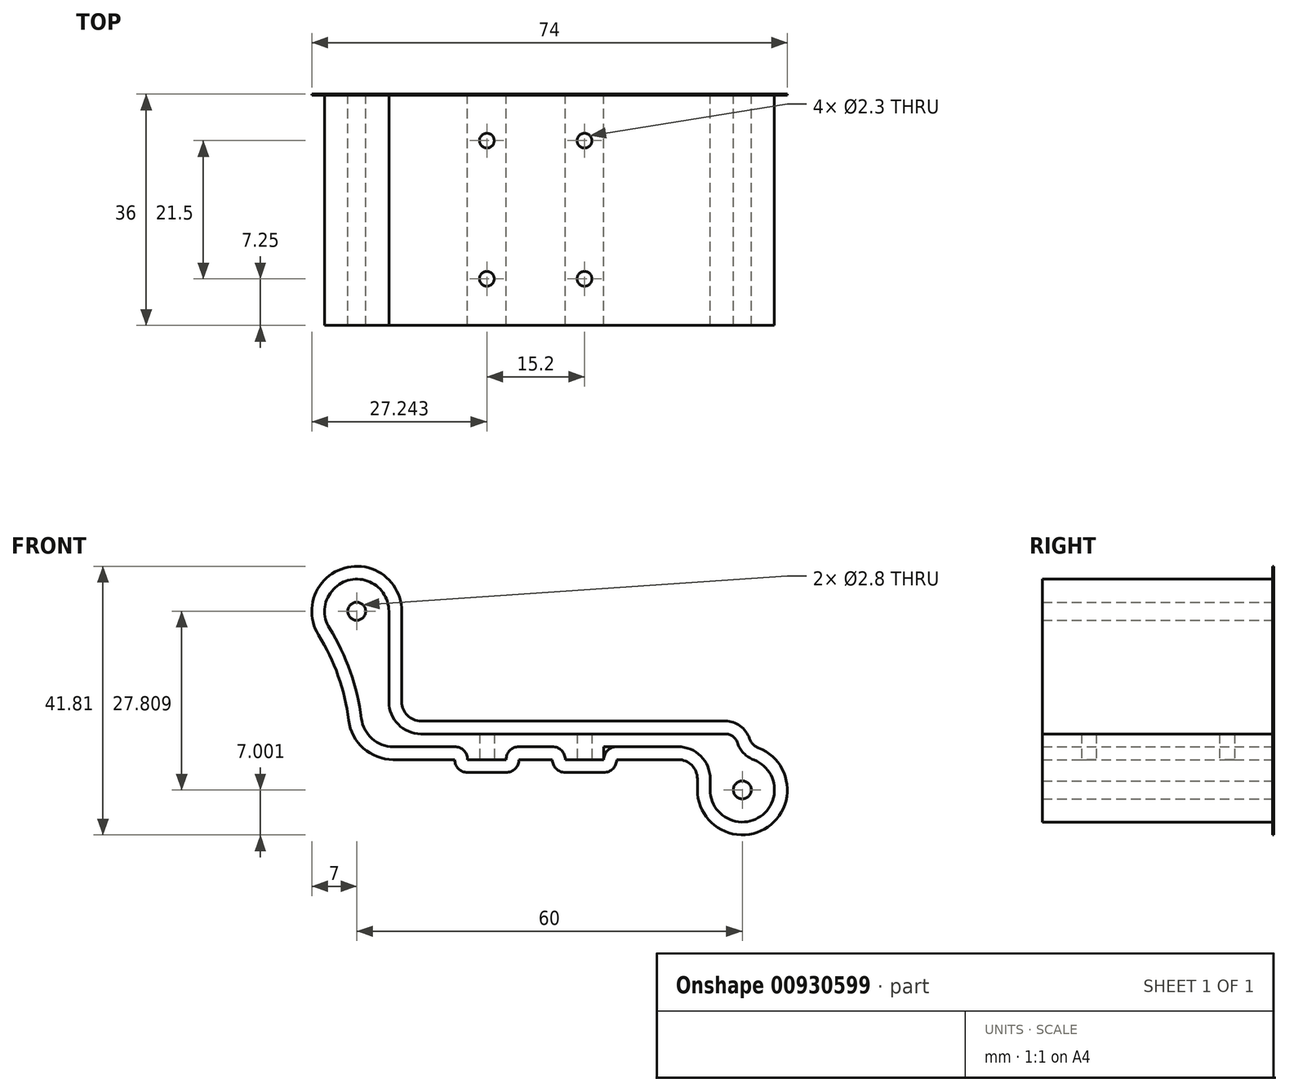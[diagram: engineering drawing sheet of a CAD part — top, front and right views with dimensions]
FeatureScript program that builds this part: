
annotation { "Feature Type Name" : "Feature", "Feature Type Description" : "" }
export const myFeature = defineFeature(function(context is Context, id is Id, definition is map)
    precondition{}
    {
        {
            var Q0;
            Q0=qCreatedBy(makeId("Front.planeOp"),FACE);
            var sketch = newSketch(context, id + "F0", { "sketchPlane" : qUnion([Q0])});
            skCircle(sketch, "E0", {"center": v(0, 0) * mm, "radius": 1.4 * mm});
            skCircle(sketch, "E1", {"center": v(60, -27.8) * mm, "radius": 1.4 * mm});
            skCircle(sketch, "E2", {"center": v(35, -55.09) * mm, "radius": 29 * mm, "construction": true});
            skArc(sketch, "E3", {"start": v(55, -27.8) * mm, "mid": v(62.83, -31.93) * mm, "end": v(61.79, -23.14) * mm});
            skLineSegment(sketch, "E4", {"start": v(1, -21.09) * mm, "end": v(55, -21.09) * mm});
            skLineSegment(sketch, "E5", {"start": v(55, -21.09) * mm, "end": v(55, -27.8) * mm});
            skArc(sketch, "E6", {"start": v(1, -21.09) * mm, "mid": v(-0.34, -11.5) * mm, "end": v(-4.25, -2.63) * mm});
            skArc(sketch, "E7", {"start": v(59, -19.09) * mm, "mid": v(59.76, -21.55) * mm, "end": v(61.79, -23.14) * mm});
            skLineSegment(sketch, "E8", {"start": v(5, -19.09) * mm, "end": v(5, 0) * mm});
            skLineSegment(sketch, "E9.trimOffspring", {"start": v(5, -19.09) * mm, "end": v(59, -19.09) * mm});
            skArc(sketch, "E10.trimOffspring", {"start": v(5, 0) * mm, "mid": v(-1.37, 4.8) * mm, "end": v(-4.25, -2.63) * mm});
            skSolve(sketch);
        }
        {
            var Q0;
            Q0=qSketchRegion(id+"F0",true);
            extrude(context, id + "F1", {"entities" : qUnion([Q0]), "depth" : 36 * mm});
        }
        {
            var Q0;
            Q0=makeQuery(id+"F1.opExtrude","SWEPT_EDGE",EDGE,{"disambiguationData":[OSD([sQuery(id+"F0.wireOp",EDGE,"E8"),sQuery(id+"F0.wireOp",EDGE,"E9.trimOffspring")])]});
            var Q1;
            Q1=makeQuery(id+"F1.opExtrude","SWEPT_EDGE",EDGE,{"disambiguationData":[OSD([sQuery(id+"F0.wireOp",EDGE,"E4"),sQuery(id+"F0.wireOp",EDGE,"E6")])]});
            var Q2;
            Q2=makeQuery(id+"F1.opExtrude","SWEPT_EDGE",EDGE,{"disambiguationData":[OSD([sQuery(id+"F0.wireOp",EDGE,"E4"),sQuery(id+"F0.wireOp",EDGE,"E5")])]});
            fillet(context, id + "F2", {"entities" : qUnion([Q0, Q1, Q2]), "radius" : 5 * mm, "tangentPropagation" : true, "allowEdgeOverflow" : false});
        }
        {
            var Q0;
            Q0=makeQuery(id+"F1.opExtrude","SWEPT_FACE",FACE,{"disambiguationData":[OSD([sQuery(id+"F0.wireOp",EDGE,"E4")])]});
            var sketch = newSketch(context, id + "F3", { "sketchPlane" : qUnion([Q0])});
            skLineSegment(sketch, "E11", {"start": v(5.69, 18) * mm, "end": v(50, 18) * mm, "construction": true});
            skLineSegment(sketch, "E12", {"start": v(27.84, 36) * mm, "end": v(27.84, 0) * mm, "construction": true});
            skLineSegment(sketch, "E13.bottom", {"start": v(17.64, 31.5) * mm, "end": v(38.04, 31.5) * mm, "construction": true});
            skLineSegment(sketch, "E13.top", {"start": v(17.64, 4.5) * mm, "end": v(38.04, 4.5) * mm, "construction": true});
            skLineSegment(sketch, "E13.left", {"start": v(17.64, 31.5) * mm, "end": v(17.64, 4.5) * mm, "construction": true});
            skLineSegment(sketch, "E13.right", {"start": v(38.04, 31.5) * mm, "end": v(38.04, 4.5) * mm, "construction": true});
            skCircle(sketch, "E14", {"center": v(20.24, 28.75) * mm, "radius": 3 * mm, "construction": true});
            skCircle(sketch, "E15", {"center": v(35.44, 28.75) * mm, "radius": 3 * mm, "construction": true});
            skCircle(sketch, "E16", {"center": v(20.24, 7.25) * mm, "radius": 3 * mm, "construction": true});
            skCircle(sketch, "E17", {"center": v(35.44, 7.25) * mm, "radius": 3 * mm, "construction": true});
            skLineSegment(sketch, "E18.bottom", {"start": v(17.24, 36) * mm, "end": v(23.24, 36) * mm});
            skLineSegment(sketch, "E18.top", {"start": v(17.24, 0) * mm, "end": v(23.24, 0) * mm});
            skLineSegment(sketch, "E18.left", {"start": v(17.24, 36) * mm, "end": v(17.24, 0) * mm});
            skLineSegment(sketch, "E18.right", {"start": v(23.24, 36) * mm, "end": v(23.24, 0) * mm});
            skLineSegment(sketch, "E19.bottom", {"start": v(32.44, 36) * mm, "end": v(38.44, 36) * mm});
            skLineSegment(sketch, "E19.top", {"start": v(32.44, 0) * mm, "end": v(38.44, 0) * mm});
            skLineSegment(sketch, "E19.left", {"start": v(32.44, 36) * mm, "end": v(32.44, 0) * mm});
            skLineSegment(sketch, "E19.right", {"start": v(38.44, 36) * mm, "end": v(38.44, 0) * mm});
            skSolve(sketch);
        }
        {
            var Q0;
            Q0=qSketchRegion(id+"F3",true);
            extrude(context, id + "F4", {"entities" : qUnion([Q0]), "operationType" : NewBodyOperationType.ADD, "depth" : 2 * mm});
        }
        {
            var Q0;
            Q0=makeQuery(id+"F1.opExtrude","SWEPT_EDGE",EDGE,{"disambiguationData":[OSD([sQuery(id+"F0.wireOp",EDGE,"E7"),sQuery(id+"F0.wireOp",EDGE,"E9.trimOffspring")])]});
            fillet(context, id + "F5", {"entities" : qUnion([Q0]), "radius" : 2 * mm, "tangentPropagation" : true, "allowEdgeOverflow" : false});
        }
        {
            var Q0;
            Q0=makeQuery(id+"F4.opExtrude","CAP_FACE",FACE,{"disambiguationData":[OSD([sQuery(id+"F3.wireOp",EDGE,"E18.bottom"),sQuery(id+"F3.wireOp",EDGE,"E18.top"),sQuery(id+"F3.wireOp",EDGE,"E18.left"),sQuery(id+"F3.wireOp",EDGE,"E18.right")])],"isStart":false});
            var sketch = newSketch(context, id + "F6", { "sketchPlane" : qUnion([Q0])});
            skLineSegment(sketch, "E20", {"start": v(17.24, 18) * mm, "end": v(38.44, 18) * mm, "construction": true});
            skCircle(sketch, "E21", {"center": v(20.24, 28.75) * mm, "radius": 1.15 * mm});
            skCircle(sketch, "E22", {"center": v(35.44, 28.75) * mm, "radius": 1.15 * mm});
            skCircle(sketch, "E23", {"center": v(20.24, 7.25) * mm, "radius": 1.15 * mm});
            skCircle(sketch, "E24", {"center": v(35.44, 7.25) * mm, "radius": 1.15 * mm});
            skSolve(sketch);
        }
        {
            var Q0;
            Q0=qSketchRegion(id+"F6",true);
            extrude(context, id + "F7", {"entities" : qUnion([Q0]), "operationType" : NewBodyOperationType.REMOVE, "endBound" : BoundingType.UP_TO_NEXT, "oppositeDirection" : true, "depth" : 25 * mm, "offsetDistance" : 25 * mm});
        }
        {
            var Q0;
            Q0=makeQuery(id+"F4.opExtrude","CAP_EDGE",EDGE,{"disambiguationData":[OSD([sQuery(id+"F3.wireOp",EDGE,"E18.left")])],"isStart":true});
            var Q1;
            Q1=makeQuery(id+"F4.opExtrude","CAP_EDGE",EDGE,{"disambiguationData":[OSD([sQuery(id+"F3.wireOp",EDGE,"E18.right")])],"isStart":true});
            var Q2;
            Q2=makeQuery(id+"F4.opExtrude","CAP_EDGE",EDGE,{"disambiguationData":[OSD([sQuery(id+"F3.wireOp",EDGE,"E19.left")])],"isStart":true});
            var Q3;
            Q3=makeQuery(id+"F4.opExtrude","CAP_EDGE",EDGE,{"disambiguationData":[OSD([sQuery(id+"F3.wireOp",EDGE,"E19.right")])],"isStart":true});
            fillet(context, id + "F8", {"entities" : qUnion([Q0, Q1, Q2, Q3]), "radius" : 2 * mm, "tangentPropagation" : true, "allowEdgeOverflow" : false});
        }
        {
            var Q0;
            Q0=qCreatedBy(makeId("Front.planeOp"),FACE);
            var sketch = newSketch(context, id + "F9", { "sketchPlane" : qUnion([Q0])});
            skArc(sketch, "E25", {"start": v(5, 0) * mm, "mid": v(-1.37, 4.8) * mm, "end": v(-4.25, -2.63) * mm});
            skArc(sketch, "E26", {"start": v(0.73, -16.7) * mm, "mid": v(2.38, -19.83) * mm, "end": v(5.69, -21.09) * mm});
            skArc(sketch, "E27", {"start": v(5, -14.09) * mm, "mid": v(6.46, -17.62) * mm, "end": v(10, -19.09) * mm});
            skArc(sketch, "E28", {"start": v(55, -26.09) * mm, "mid": v(53.54, -22.55) * mm, "end": v(50, -21.09) * mm});
            skArc(sketch, "E29", {"start": v(55, -27.8) * mm, "mid": v(62.83, -31.93) * mm, "end": v(61.79, -23.14) * mm});
            skArc(sketch, "E30", {"start": v(59.22, -20.45) * mm, "mid": v(58.5, -19.46) * mm, "end": v(57.32, -19.09) * mm});
            skArc(sketch, "E31", {"start": v(59.22, -20.45) * mm, "mid": v(60.2, -22.09) * mm, "end": v(61.79, -23.14) * mm});
            skLineSegment(sketch, "E32", {"start": v(10, -19.09) * mm, "end": v(57.32, -19.09) * mm});
            skLineSegment(sketch, "E33", {"start": v(55, -26.09) * mm, "end": v(55, -27.8) * mm});
            skLineSegment(sketch, "E34", {"start": v(50, -21.09) * mm, "end": v(40.44, -21.09) * mm});
            skLineSegment(sketch, "E35", {"start": v(32.44, -23.09) * mm, "end": v(38.44, -23.09) * mm});
            skLineSegment(sketch, "E36", {"start": v(30.44, -21.09) * mm, "end": v(25.24, -21.09) * mm});
            skLineSegment(sketch, "E37", {"start": v(23.24, -23.09) * mm, "end": v(17.24, -23.09) * mm});
            skLineSegment(sketch, "E38", {"start": v(15.24, -21.09) * mm, "end": v(5.69, -21.09) * mm});
            skLineSegment(sketch, "E39", {"start": v(5, 0) * mm, "end": v(5, -14.09) * mm});
            skArc(sketch, "E40", {"start": v(17.24, -23.09) * mm, "mid": v(16.66, -21.67) * mm, "end": v(15.24, -21.09) * mm});
            skArc(sketch, "E41", {"start": v(25.24, -21.09) * mm, "mid": v(23.83, -21.67) * mm, "end": v(23.24, -23.09) * mm});
            skArc(sketch, "E42", {"start": v(32.44, -23.09) * mm, "mid": v(31.86, -21.67) * mm, "end": v(30.44, -21.09) * mm});
            skArc(sketch, "E43", {"start": v(40.44, -21.09) * mm, "mid": v(39.03, -21.67) * mm, "end": v(38.44, -23.09) * mm});
            skArc(sketch, "E44", {"start": v(0.73, -16.7) * mm, "mid": v(-1, -9.4) * mm, "end": v(-4.25, -2.63) * mm});
            skArc(sketch, "E45", {"start": v(7, 0) * mm, "mid": v(-1.92, 6.73) * mm, "end": v(-5.95, -3.69) * mm});
            skArc(sketch, "E46", {"start": v(-1.26, -16.96) * mm, "mid": v(-2.89, -10.07) * mm, "end": v(-5.95, -3.69) * mm});
            skLineSegment(sketch, "E47", {"start": v(7, 0) * mm, "end": v(7, -14.09) * mm});
            skArc(sketch, "E48", {"start": v(7, -14.09) * mm, "mid": v(7.88, -16.2) * mm, "end": v(10, -17.09) * mm});
            skLineSegment(sketch, "E49", {"start": v(10, -17.09) * mm, "end": v(57.32, -17.09) * mm});
            skArc(sketch, "E50", {"start": v(61.12, -19.82) * mm, "mid": v(59.66, -17.84) * mm, "end": v(57.32, -17.09) * mm});
            skArc(sketch, "E51", {"start": v(61.12, -19.82) * mm, "mid": v(61.65, -20.7) * mm, "end": v(62.5, -21.27) * mm});
            skArc(sketch, "E52", {"start": v(53, -27.8) * mm, "mid": v(63.97, -33.58) * mm, "end": v(62.5, -21.27) * mm});
            skLineSegment(sketch, "E53", {"start": v(53, -27.8) * mm, "end": v(53, -26.09) * mm});
            skArc(sketch, "E54", {"start": v(53, -26.09) * mm, "mid": v(52.12, -23.96) * mm, "end": v(50, -23.09) * mm});
            skLineSegment(sketch, "E55", {"start": v(50, -23.09) * mm, "end": v(40.44, -23.09) * mm});
            skLineSegment(sketch, "E56", {"start": v(32.44, -25.09) * mm, "end": v(38.44, -25.09) * mm});
            skLineSegment(sketch, "E57", {"start": v(25.24, -23.09) * mm, "end": v(30.44, -23.09) * mm});
            skLineSegment(sketch, "E58", {"start": v(23.24, -25.09) * mm, "end": v(17.24, -25.09) * mm});
            skLineSegment(sketch, "E59", {"start": v(15.24, -23.09) * mm, "end": v(5.69, -23.09) * mm});
            skArc(sketch, "E60", {"start": v(-1.26, -16.96) * mm, "mid": v(1.06, -21.33) * mm, "end": v(5.69, -23.09) * mm});
            skArc(sketch, "E61", {"start": v(15.24, -23.09) * mm, "mid": v(15.83, -24.5) * mm, "end": v(17.24, -25.09) * mm});
            skArc(sketch, "E62", {"start": v(23.24, -25.09) * mm, "mid": v(24.66, -24.5) * mm, "end": v(25.24, -23.09) * mm});
            skArc(sketch, "E63", {"start": v(30.44, -23.09) * mm, "mid": v(31.03, -24.5) * mm, "end": v(32.44, -25.09) * mm});
            skArc(sketch, "E64", {"start": v(38.44, -25.09) * mm, "mid": v(39.86, -24.5) * mm, "end": v(40.44, -23.09) * mm});
            skSolve(sketch);
        }
        {
            var Q0;
            Q0=qSketchRegion(id+"F9",true);
            extrude(context, id + "F10", {"entities" : qUnion([Q0]), "operationType" : NewBodyOperationType.ADD, "depth" : 0.2 * mm, "offsetDistance" : 25 * mm});
        }
    });
